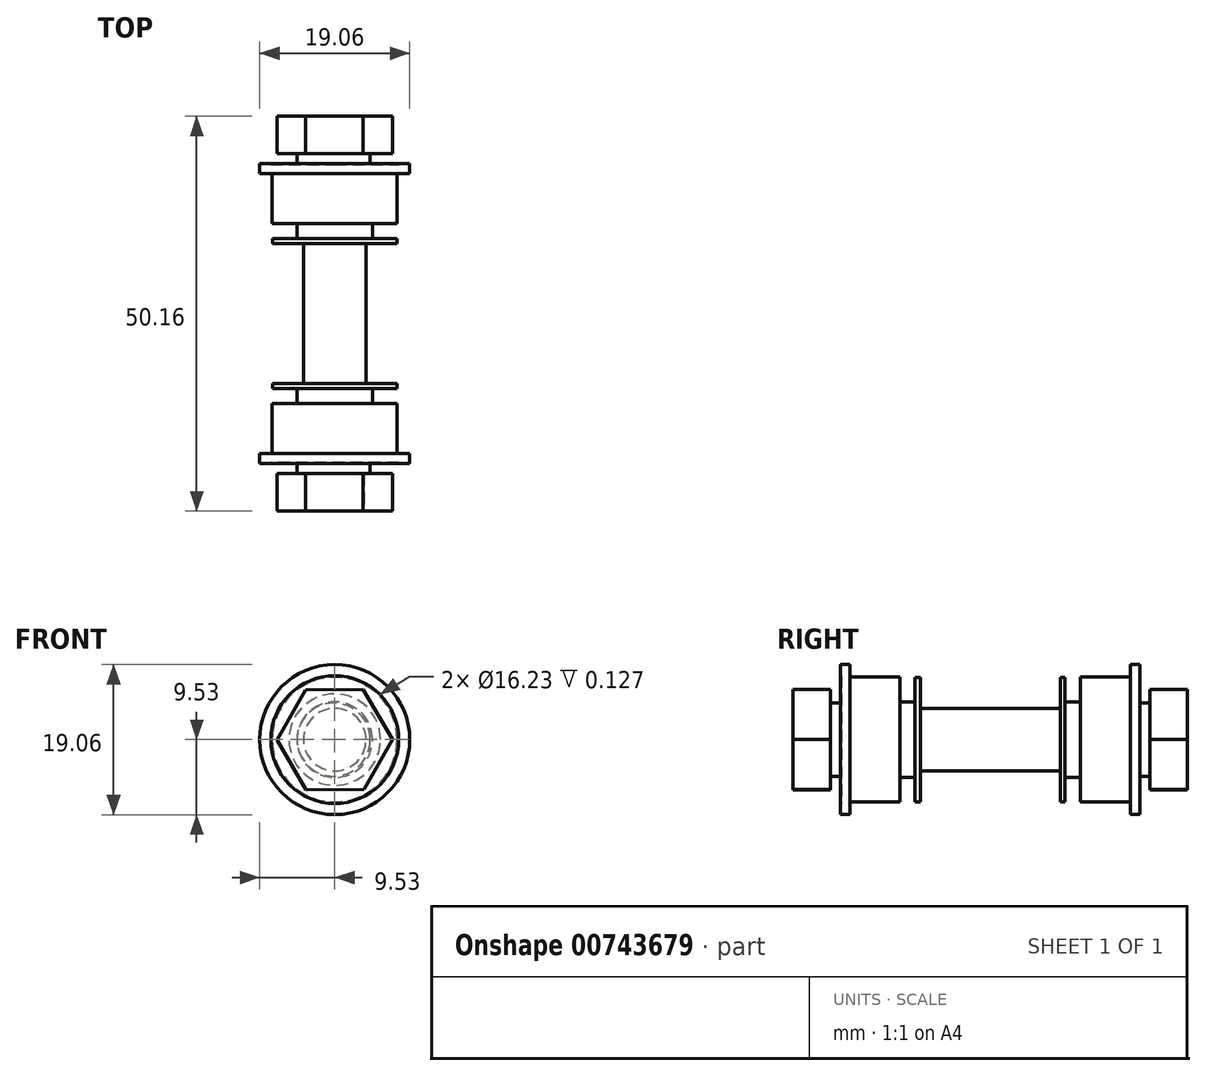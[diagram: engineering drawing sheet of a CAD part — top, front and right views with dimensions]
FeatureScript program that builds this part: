
annotation { "Feature Type Name" : "Feature", "Feature Type Description" : "" }
export const myFeature = defineFeature(function(context is Context, id is Id, definition is map)
    precondition{}
    {
        {
            var Q0;
            Q0=qCreatedBy(makeId("Front.planeOp"),FACE);
            var sketch = newSketch(context, id + "F0", { "sketchPlane" : qUnion([Q0])});
            skCircle(sketch, "E0.cCircle", {"center": v(0, 0) * mm, "radius": 6.35 * mm, "construction": true});
            skLineSegment(sketch, "E0.0", {"start": v(-7.33, -0.04) * mm, "end": v(-3.7, 6.33) * mm});
            skLineSegment(sketch, "E0.1", {"start": v(-3.7, 6.33) * mm, "end": v(3.63, 6.37) * mm});
            skLineSegment(sketch, "E0.2", {"start": v(3.63, 6.37) * mm, "end": v(7.33, 0.04) * mm});
            skLineSegment(sketch, "E0.3", {"start": v(7.33, 0.04) * mm, "end": v(3.7, -6.33) * mm});
            skLineSegment(sketch, "E0.4", {"start": v(3.7, -6.33) * mm, "end": v(-3.63, -6.37) * mm});
            skLineSegment(sketch, "E0.5", {"start": v(-3.63, -6.37) * mm, "end": v(-7.33, -0.04) * mm});
            skPoint(sketch, "E0.0.midPoint", {"position": v(-5.52, 3.14) * mm});
            skSolve(sketch);
        }
        {
            var Q0;
            Q0=qSketchRegion(id+"F0",true);
            extrude(context, id + "F1", {"entities" : qUnion([Q0]), "depth" : 4.76 * mm, "offsetDistance" : 25.4 * mm});
        }
        {
            var Q0;
            Q0=makeQuery(id+"F1.opExtrude","CAP_FACE",FACE,{"disambiguationData":[OSD([sQuery(id+"F0.wireOp",EDGE,"E0.0"),sQuery(id+"F0.wireOp",EDGE,"E0.1"),sQuery(id+"F0.wireOp",EDGE,"E0.2"),sQuery(id+"F0.wireOp",EDGE,"E0.3"),sQuery(id+"F0.wireOp",EDGE,"E0.4"),sQuery(id+"F0.wireOp",EDGE,"E0.5")])],"isStart":false});
            var sketch = newSketch(context, id + "F2", { "sketchPlane" : qUnion([Q0])});
            skCircle(sketch, "E1", {"center": v(0, 0) * mm, "radius": 3.97 * mm});
            skSolve(sketch);
        }
        {
            var Q0;
            Q0=qSketchRegion(id+"F2",true);
            extrude(context, id + "F3", {"entities" : qUnion([Q0]), "operationType" : NewBodyOperationType.ADD, "depth" : 20.32 * mm, "offsetDistance" : 25.4 * mm});
        }
        {
            var Q0;
            Q0=makeQuery(id+"F1.opExtrude","CAP_FACE",FACE,{"disambiguationData":[OSD([sQuery(id+"F0.wireOp",EDGE,"E0.0"),sQuery(id+"F0.wireOp",EDGE,"E0.1"),sQuery(id+"F0.wireOp",EDGE,"E0.2"),sQuery(id+"F0.wireOp",EDGE,"E0.3"),sQuery(id+"F0.wireOp",EDGE,"E0.4"),sQuery(id+"F0.wireOp",EDGE,"E0.5")])],"isStart":false});
            var sketch = newSketch(context, id + "F4", { "sketchPlane" : qUnion([Q0])});
            skCircle(sketch, "E2", {"center": v(-0.13, 0) * mm, "radius": 4.65 * mm});
            skSolve(sketch);
        }
        {
            var Q0;
            Q0=qSketchRegion(id+"F4",true);
            extrude(context, id + "F5", {"entities" : qUnion([Q0]), "operationType" : NewBodyOperationType.ADD, "depth" : 1.27 * mm, "offsetDistance" : 25.4 * mm});
        }
        {
            var Q0;
            Q0=makeQuery(id+"F5.opExtrude","CAP_FACE",FACE,{"disambiguationData":[OSD([sQuery(id+"F4.wireOp",EDGE,"E2")])],"isStart":false});
            var sketch = newSketch(context, id + "F6", { "sketchPlane" : qUnion([Q0])});
            skCircle(sketch, "E3", {"center": v(0, 0) * mm, "radius": 9.53 * mm});
            skSolve(sketch);
        }
        {
            var Q0;
            Q0=qSketchRegion(id+"F6",true);
            extrude(context, id + "F7", {"entities" : qUnion([Q0]), "operationType" : NewBodyOperationType.ADD, "depth" : 1.27 * mm, "offsetDistance" : 25.4 * mm});
        }
        {
            var Q0;
            Q0=makeQuery(id+"F7.opExtrude","CAP_FACE",FACE,{"disambiguationData":[OSD([sQuery(id+"F6.wireOp",EDGE,"E3")])],"isStart":true});
            var sketch = newSketch(context, id + "F8", { "sketchPlane" : qUnion([Q0])});
            skCircle(sketch, "E4", {"center": v(0, 0) * mm, "radius": 8.12 * mm});
            skCircle(sketch, "E5", {"center": v(0, 0) * mm, "radius": 5.81 * mm});
            skSolve(sketch);
        }
        {
            var Q0;
            Q0=qSketchRegion(id+"F8",true);
            extrude(context, id + "F9", {"entities" : qUnion([Q0]), "operationType" : NewBodyOperationType.REMOVE, "oppositeDirection" : true, "depth" : 0.13 * mm, "offsetDistance" : 25.4 * mm});
        }
        {
            var Q0;
            Q0=makeQuery(id+"F7.opExtrude","CAP_FACE",FACE,{"disambiguationData":[OSD([sQuery(id+"F6.wireOp",EDGE,"E3")])],"isStart":false});
            var sketch = newSketch(context, id + "F10", { "sketchPlane" : qUnion([Q0])});
            skCircle(sketch, "E6", {"center": v(0, 0) * mm, "radius": 7.94 * mm});
            skSolve(sketch);
        }
        {
            var Q0;
            Q0=qSketchRegion(id+"F10",true);
            extrude(context, id + "F11", {"entities" : qUnion([Q0]), "operationType" : NewBodyOperationType.ADD, "depth" : 6.35 * mm, "offsetDistance" : 25.4 * mm});
        }
        {
            var Q0;
            Q0=makeQuery(id+"F11.opExtrude","CAP_FACE",FACE,{"disambiguationData":[OSD([sQuery(id+"F10.wireOp",EDGE,"E6")])],"isStart":false});
            var sketch = newSketch(context, id + "F12", { "sketchPlane" : qUnion([Q0])});
            skCircle(sketch, "E7", {"center": v(0, 0) * mm, "radius": 4.8 * mm});
            skSolve(sketch);
        }
        {
            var Q0;
            Q0=qSketchRegion(id+"F12",true);
            extrude(context, id + "F13", {"entities" : qUnion([Q0]), "operationType" : NewBodyOperationType.ADD, "depth" : 1.9 * mm, "offsetDistance" : 25.4 * mm});
        }
        {
            var Q0;
            Q0=makeQuery(id+"F13.opExtrude","CAP_FACE",FACE,{"disambiguationData":[OSD([sQuery(id+"F12.wireOp",EDGE,"E7")])],"isStart":false});
            var sketch = newSketch(context, id + "F14", { "sketchPlane" : qUnion([Q0])});
            skCircle(sketch, "E8", {"center": v(0, 0) * mm, "radius": 7.92 * mm});
            skSolve(sketch);
        }
        {
            var Q0;
            Q0=qSketchRegion(id+"F14",true);
            extrude(context, id + "F15", {"entities" : qUnion([Q0]), "operationType" : NewBodyOperationType.ADD, "depth" : 0.64 * mm, "offsetDistance" : 25.4 * mm});
        }
        {
            var Q0;
            Q0=makeQuery(id+"F1.opExtrude","SWEPT_BODY",BODY,{"disambiguationData":[OSD([sQuery(id+"F0.wireOp",EDGE,"E0.0"),sQuery(id+"F0.wireOp",EDGE,"E0.1"),sQuery(id+"F0.wireOp",EDGE,"E0.2"),sQuery(id+"F0.wireOp",EDGE,"E0.3"),sQuery(id+"F0.wireOp",EDGE,"E0.4"),sQuery(id+"F0.wireOp",EDGE,"E0.5")])]});
            var Q1;
            Q1=makeQuery(id+"F3.opExtrude","CAP_FACE",FACE,{"disambiguationData":[OSD([sQuery(id+"F2.wireOp",EDGE,"E1")])],"isStart":false});
            mirror(context, id + "F16", {"operationType" : NewBodyOperationType.ADD, "entities" : qUnion([Q0]), "mirrorPlane" : qUnion([Q1])});
        }
    });
